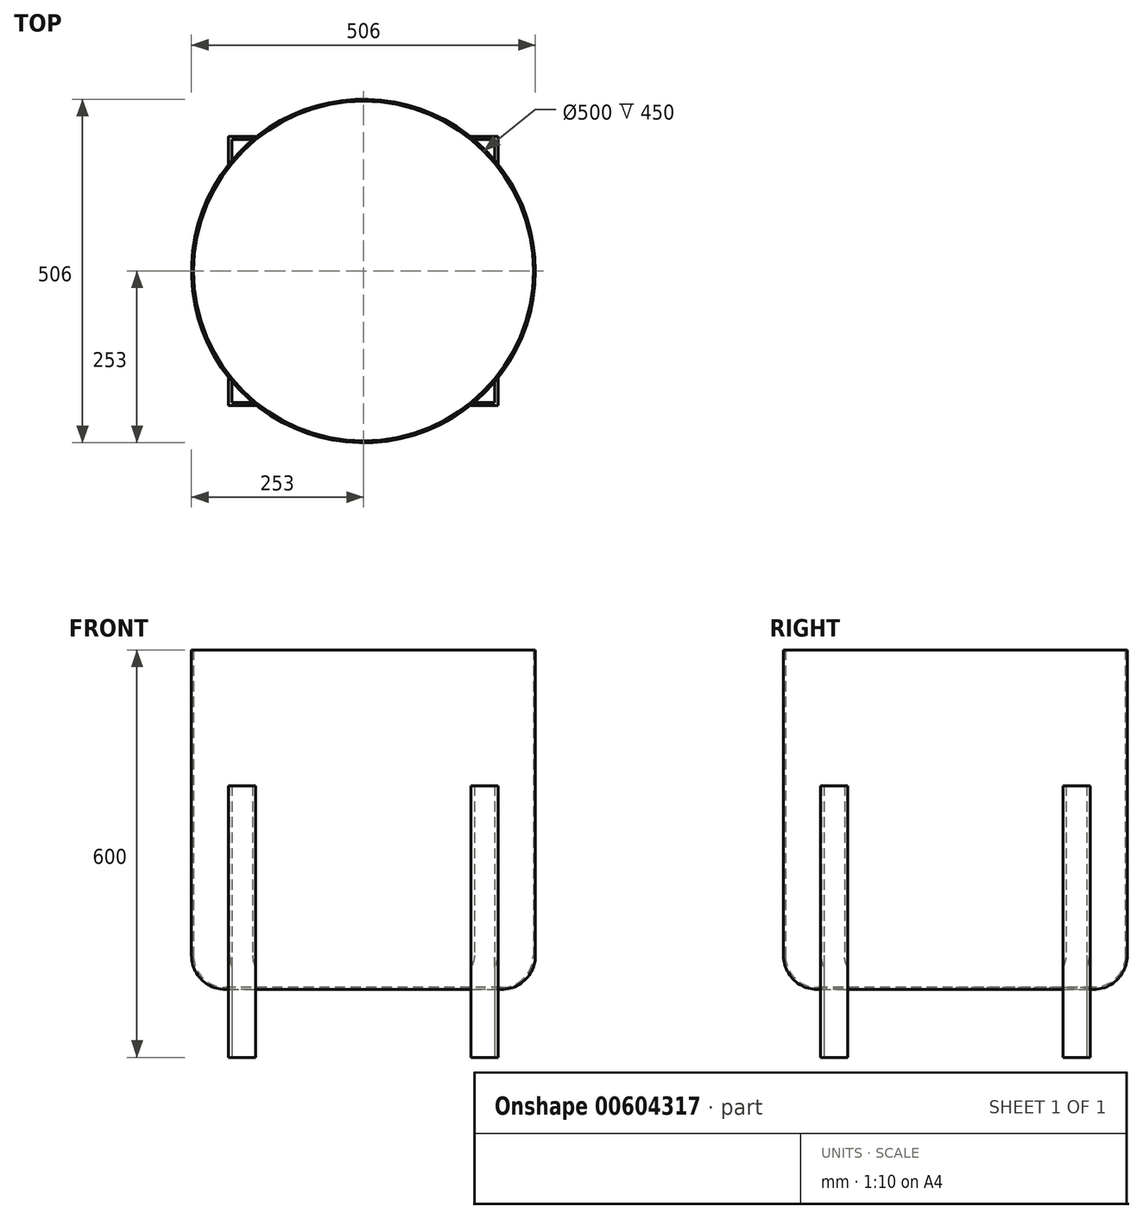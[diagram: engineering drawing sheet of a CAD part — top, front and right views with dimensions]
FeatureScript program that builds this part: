
annotation { "Feature Type Name" : "Feature", "Feature Type Description" : "" }
export const myFeature = defineFeature(function(context is Context, id is Id, definition is map)
    precondition{}
    {
        {
            var Q0;
            Q0=qCreatedBy(makeId("Top.planeOp"),FACE);
            var sketch = newSketch(context, id + "F0", { "sketchPlane" : qUnion([Q0])});
            skCircle(sketch, "E0", {"center": v(0, 0) * mm, "radius": 253 * mm});
            skSolve(sketch);
        }
        {
            var Q0;
            Q0 = qSketchRegion(id + "F0", true);
            extrude(context, id + "F1", {"entities" : qUnion([Q0]), "depth" : 500 * mm, "offsetDistance" : 25 * mm});
        }
        {
            var Q0;
            Q0=makeQuery(id+"F1.opExtrude","CAP_EDGE",EDGE,{"disambiguationData":[OSD([sQuery(id+"F0.wireOp",EDGE,"E0")])],"isStart":true});
            fillet(context, id + "F2", {"entities" : qUnion([Q0]), "radius" : 50 * mm, "tangentPropagation" : true, "allowEdgeOverflow" : false});
        }
        {
            var Q0;
            Q0=makeQuery(id+"F1.opExtrude","CAP_FACE",FACE,{"disambiguationData":[OSD([sQuery(id+"F0.wireOp",EDGE,"E0")])],"isStart":false});
            shell(context, id + "F3", {"entities" : qUnion([Q0]), "thickness" : 3 * mm});
        }
        {
            var Q0;
            Q0=qCreatedBy(makeId("Top.planeOp"),FACE);
            var sketch = newSketch(context, id + "F4", { "sketchPlane" : qUnion([Q0])});
            skLineSegment(sketch, "E1", {"start": v(-158.4, 198.4) * mm, "end": v(-198.4, 198.4) * mm});
            skLineSegment(sketch, "E2", {"start": v(-198.4, 198.4) * mm, "end": v(-198.4, 158.4) * mm});
            skLineSegment(sketch, "E3", {"start": v(-198.4, 158.4) * mm, "end": v(-193.4, 158.4) * mm});
            skLineSegment(sketch, "E4", {"start": v(-193.4, 158.4) * mm, "end": v(-193.4, 193.4) * mm});
            skLineSegment(sketch, "E5", {"start": v(-193.4, 193.4) * mm, "end": v(-158.4, 193.4) * mm});
            skLineSegment(sketch, "E6", {"start": v(-158.4, 193.4) * mm, "end": v(-158.4, 198.4) * mm});
            skLineSegment(sketch, "E7.MirrorCS", {"start": v(158.4, 193.4) * mm, "end": v(158.4, 198.4) * mm});
            skLineSegment(sketch, "E8.MirrorCS", {"start": v(198.4, 158.4) * mm, "end": v(193.4, 158.4) * mm});
            skLineSegment(sketch, "E9.MirrorCS", {"start": v(198.4, 198.4) * mm, "end": v(198.4, 158.4) * mm});
            skLineSegment(sketch, "E10.MirrorCS", {"start": v(158.4, 198.4) * mm, "end": v(198.4, 198.4) * mm});
            skLineSegment(sketch, "E11.MirrorCS", {"start": v(193.4, 158.4) * mm, "end": v(193.4, 193.4) * mm});
            skLineSegment(sketch, "E12.MirrorCS", {"start": v(193.4, 193.4) * mm, "end": v(158.4, 193.4) * mm});
            skLineSegment(sketch, "E13.MirrorCS", {"start": v(198.4, -158.4) * mm, "end": v(193.4, -158.4) * mm});
            skLineSegment(sketch, "E14.MirrorCS", {"start": v(-198.4, -158.4) * mm, "end": v(-193.4, -158.4) * mm});
            skLineSegment(sketch, "E15.MirrorCS", {"start": v(158.4, -193.4) * mm, "end": v(158.4, -198.4) * mm});
            skLineSegment(sketch, "E16.MirrorCS", {"start": v(-158.4, -193.4) * mm, "end": v(-158.4, -198.4) * mm});
            skLineSegment(sketch, "E17.MirrorCS", {"start": v(193.4, -193.4) * mm, "end": v(158.4, -193.4) * mm});
            skLineSegment(sketch, "E18.MirrorCS", {"start": v(193.4, -158.4) * mm, "end": v(193.4, -193.4) * mm});
            skLineSegment(sketch, "E19.MirrorCS", {"start": v(158.4, -198.4) * mm, "end": v(198.4, -198.4) * mm});
            skLineSegment(sketch, "E20.MirrorCS", {"start": v(198.4, -198.4) * mm, "end": v(198.4, -158.4) * mm});
            skLineSegment(sketch, "E21.MirrorCS", {"start": v(-158.4, -198.4) * mm, "end": v(-198.4, -198.4) * mm});
            skLineSegment(sketch, "E22.MirrorCS", {"start": v(-198.4, -198.4) * mm, "end": v(-198.4, -158.4) * mm});
            skLineSegment(sketch, "E23.MirrorCS", {"start": v(-193.4, -193.4) * mm, "end": v(-158.4, -193.4) * mm});
            skLineSegment(sketch, "E24.MirrorCS", {"start": v(-193.4, -158.4) * mm, "end": v(-193.4, -193.4) * mm});
            skSolve(sketch);
        }
        {
            var Q0;
            Q0 = qSketchRegion(id + "F4", true);
            extrude(context, id + "F5", {"entities" : qUnion([Q0]), "operationType" : NewBodyOperationType.ADD, "depth" : 300 * mm, "offsetDistance" : 25 * mm, "hasSecondDirection" : true, "secondDirectionOppositeDirection" : true, "secondDirectionDepth" : 100 * mm});
        }
    });
